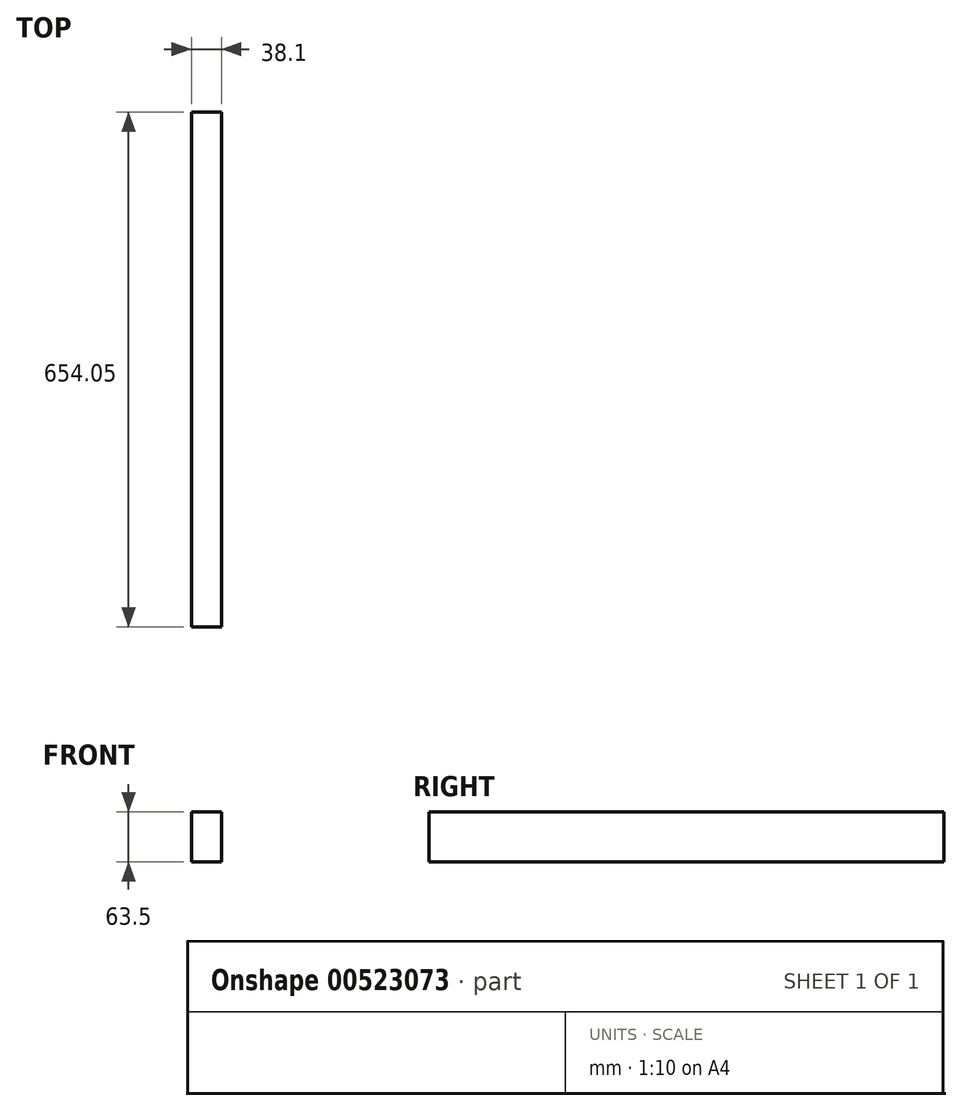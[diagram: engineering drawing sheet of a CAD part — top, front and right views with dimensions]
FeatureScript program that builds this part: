
annotation { "Feature Type Name" : "Feature", "Feature Type Description" : "" }
export const myFeature = defineFeature(function(context is Context, id is Id, definition is map)
    precondition{}
    {
        {
            var Q0;
            Q0=qCreatedBy(makeId("Front.planeOp"),FACE);
            var sketch = newSketch(context, id + "F0", { "sketchPlane" : qUnion([Q0])});
            skLineSegment(sketch, "E0.bottom", {"start": v(0, 0) * mm, "end": v(38.1, 0) * mm});
            skLineSegment(sketch, "E0.top", {"start": v(0, 63.5) * mm, "end": v(38.1, 63.5) * mm});
            skLineSegment(sketch, "E0.left", {"start": v(0, 0) * mm, "end": v(0, 63.5) * mm});
            skLineSegment(sketch, "E0.right", {"start": v(38.1, 0) * mm, "end": v(38.1, 63.5) * mm});
            skSolve(sketch);
        }
        {
            var Q0;
            Q0 = qSketchRegion(id + "F0", true);
            extrude(context, id + "F1", {"entities" : qUnion([Q0]), "depth" : 654.05 * mm, "offsetDistance" : 25.4 * mm});
        }
    });
